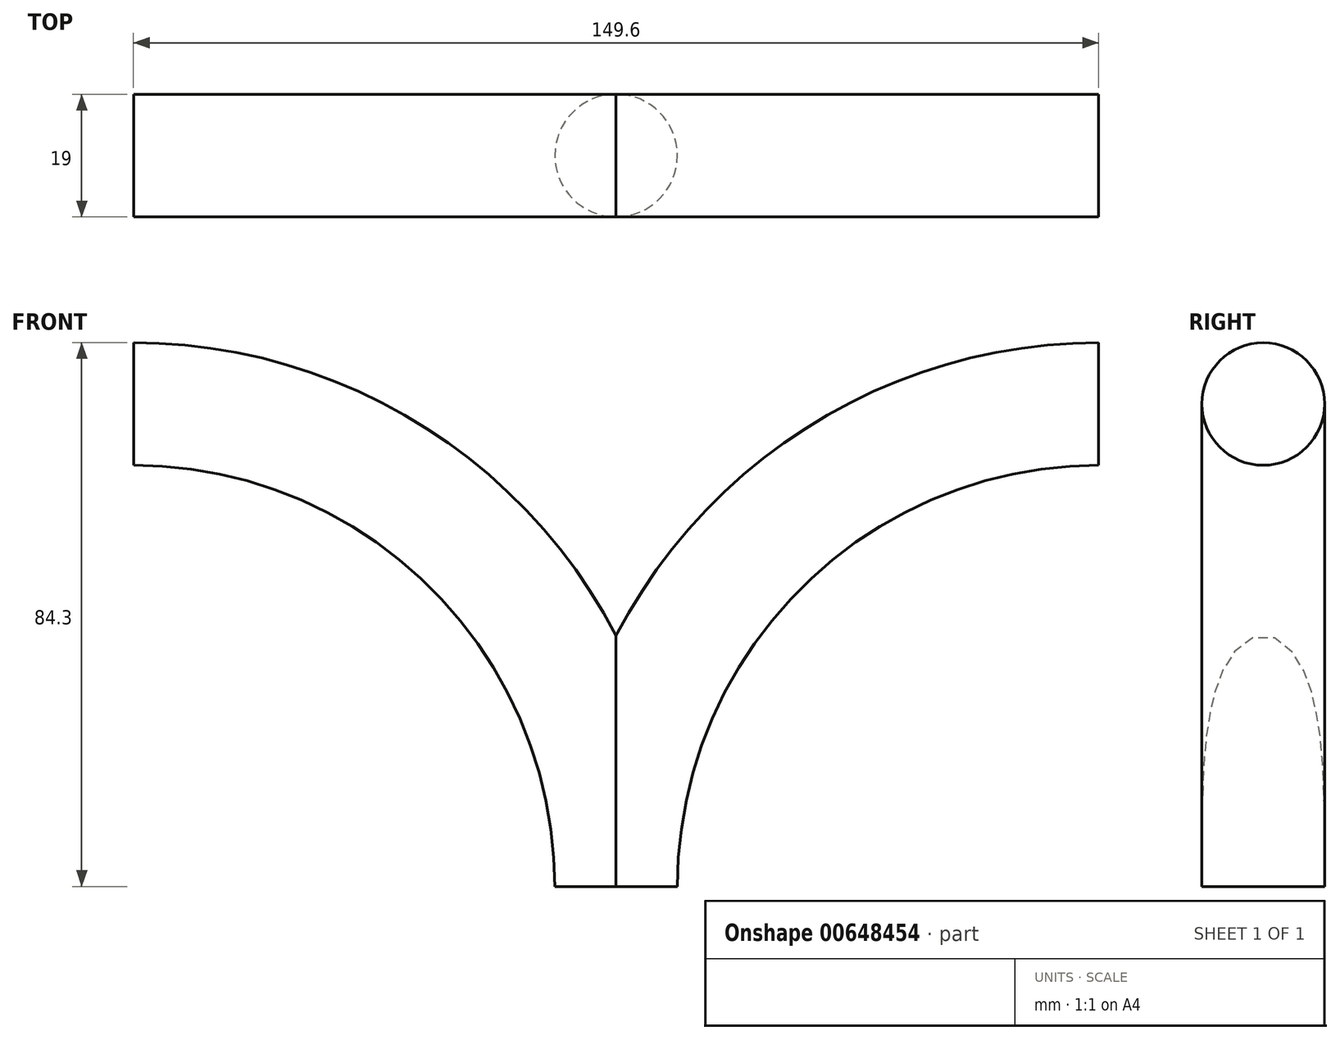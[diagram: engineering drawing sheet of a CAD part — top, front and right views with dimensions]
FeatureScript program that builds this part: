
annotation { "Feature Type Name" : "Feature", "Feature Type Description" : "" }
export const myFeature = defineFeature(function(context is Context, id is Id, definition is map)
    precondition{}
    {
        {
            var Q0;
            Q0=qCreatedBy(makeId("Top.planeOp"),FACE);
            var sketch = newSketch(context, id + "F0", { "sketchPlane" : qUnion([Q0])});
            skCircle(sketch, "E0", {"center": v(0, 0) * mm, "radius": 9.5 * mm});
            skLineSegment(sketch, "E1", {"start": v(74.8, -74.7) * mm, "end": v(74.8, 60.61) * mm});
            skLineSegment(sketch, "E2", {"start": v(9.5, 0) * mm, "end": v(74.8, 0) * mm});
            skSolve(sketch);
        }
        {
            var Q0;
            Q0=makeQuery(id+"F0.imprint","IMPRINT",FACE,{"disambiguationData":[TD([[makeQuery(id+"F0.imprint","IMPRINT",EDGE,{"derivedFrom":sQuery(id+"F0.wireOp",EDGE,"E0")}),1.0]])]});
            var Q1;
            Q1=sQuery(id+"F0.wireOp",EDGE,"E1");
            revolve(context, id + "F1", {"entities" : qUnion([Q0]), "axis" : qUnion([Q1]), "revolveType" : RevolveType.ONE_DIRECTION, "angle" : 90 * degree});
        }
        {
            var Q0;
            Q0=qCreatedBy(makeId("Right.planeOp"),FACE);
            var sketch = newSketch(context, id + "F2", { "sketchPlane" : qUnion([Q0])});
            skLineSegment(sketch, "E3.bottom", {"start": v(70.96, 67.48) * mm, "end": v(-74.74, 67.48) * mm});
            skLineSegment(sketch, "E3.top", {"start": v(70.96, -61.46) * mm, "end": v(-74.74, -61.46) * mm});
            skLineSegment(sketch, "E3.left", {"start": v(70.96, 67.48) * mm, "end": v(70.96, -61.46) * mm});
            skLineSegment(sketch, "E3.right", {"start": v(-74.74, 67.48) * mm, "end": v(-74.74, -61.46) * mm});
            skSolve(sketch);
        }
        {
            var Q0;
            Q0 = qSketchRegion(id + "F2", true);
            extrude(context, id + "F3", {"entities" : qUnion([Q0]), "operationType" : NewBodyOperationType.REMOVE, "oppositeDirection" : true, "depth" : 25 * mm, "offsetDistance" : 25 * mm});
        }
        {
            var Q0;
            Q0=makeQuery(id+"F1.opRevolve","SWEPT_BODY",BODY,{"disambiguationData":[OSD([sQuery(id+"F0.wireOp",EDGE,"E0")])]});
            var Q1;
            Q1=qCreatedBy(makeId("Right.planeOp"),FACE);
            mirror(context, id + "F4", {"operationType" : NewBodyOperationType.ADD, "entities" : qUnion([Q0]), "mirrorPlane" : qUnion([Q1])});
        }
    });
